# Revit family: golf
name_source: partatom
category: Generic Models
units: mm (PartAtom-declared; Revit-internal decimal feet)

## family parameters
Always vertical = No
Can host rebar = No
Cut with Voids When Loaded = No
Part Type = Normal
Room Calculation Point = No
Round Connector Dimension = Use Diameter
Shared = No
Work Plane-Based = No

## types (1)
- Default
    BIMobject category = Storage Unit
    BOSUseNativeGeometries = 0
    Default Elevation = 0' - 0"
    Design country = Poland
    Edition number = 1
    IFC Classification = Furniture
    Manufacturer country = Poland
    Manufacturer name = Robe Concept
    Material main = MDF
    Material secondary = Stainless steel
    Nominal height = 860
    Nominal width = 1830
    Product Guid = 61f411ec-08e4-4a26-9889-e23a424efe93
    Product SKU = golf
    Product data url = https://bimobject.com
    Product name = Golf
    QR code = http://bimobject.com
    UNSPSC Code = 56
    Uniclass 1.4 Code = L8211
    Uniclass 1.4 Description = Furniture
    Weight Net (Kg) = 70

## geometry (parser evidence)
native form markers: Sweep x1
no freeform markers — native parametric forms only
